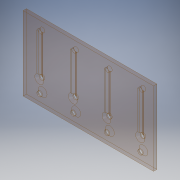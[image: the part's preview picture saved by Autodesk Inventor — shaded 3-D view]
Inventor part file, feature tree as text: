
AUTODESK INVENTOR PART (.ipt)
format: ipt  version: 2019 (Build 230136000, 136)  size: 179,712 bytes
history: native  units: in
note: dims shown in document units (in); Inventor stores cm internally (conversion verified against a paired STEP export)
features: sketch x5, hole x3, projected_geometry x3, extrude x2, pattern_linear x1
ambient origin geometry x8: Origin, YZ Plane, XZ Plane, XY Plane, X Axis, Y Axis, Z Axis, Center Point
bodies: Solid1 (feature_tree)
feature tree (14):
  extrude  "Extrusion1"  Depth=4.85in
  hole  "Hole1"  [1 undecoded]
  hole  "Hole2"  [1 undecoded]
  hole  "Hole3"  [1 undecoded]
  extrude  "Extrusion2"  Depth=1.25in
  pattern_linear  "Rectangular Pattern1"  Spacing1=0.05in  [1 undecoded]
  sketch  "Sketch1"  dims[d0=2.75in d1=4.85in]
  sketch  "Sketch2"  dims[d2=0.125in d3=0.0in d5=0.385in]
  sketch  "Sketch3"  dims[d6=0.6in d7=1.25in]
  projected_geometry  "Projected Loop1"
  sketch  "Sketch4"  dims[d8=1.25in d9=1.25in]
  projected_geometry  "Projected Loop2"
  sketch  "Sketch5"  dims[d10=0.177in d11=0.75in d12=0.385in d13=0.25in d14=0.5635in d15=1.0in d16=0.8108in d19=0.177in d20=1.717in d21=0.332in d22=0.25in d23=0.5635in d24=1.0in d25=0.8108in d26=2.0in d27=0.177in d28=1.717in d29=0.332in d30=0.25in d31=0.5635in d32=1.0in d33=0.8108in d34=0.05in d35=0.0in d36=1.5748in d38=1.25in]
  projected_geometry  "Projected Loop3"
note: 4 required parameter values undecoded (feature->parameter linkage not recoverable at this tier; creation-order binding heuristic only, values carry confidence <= 0.55)
